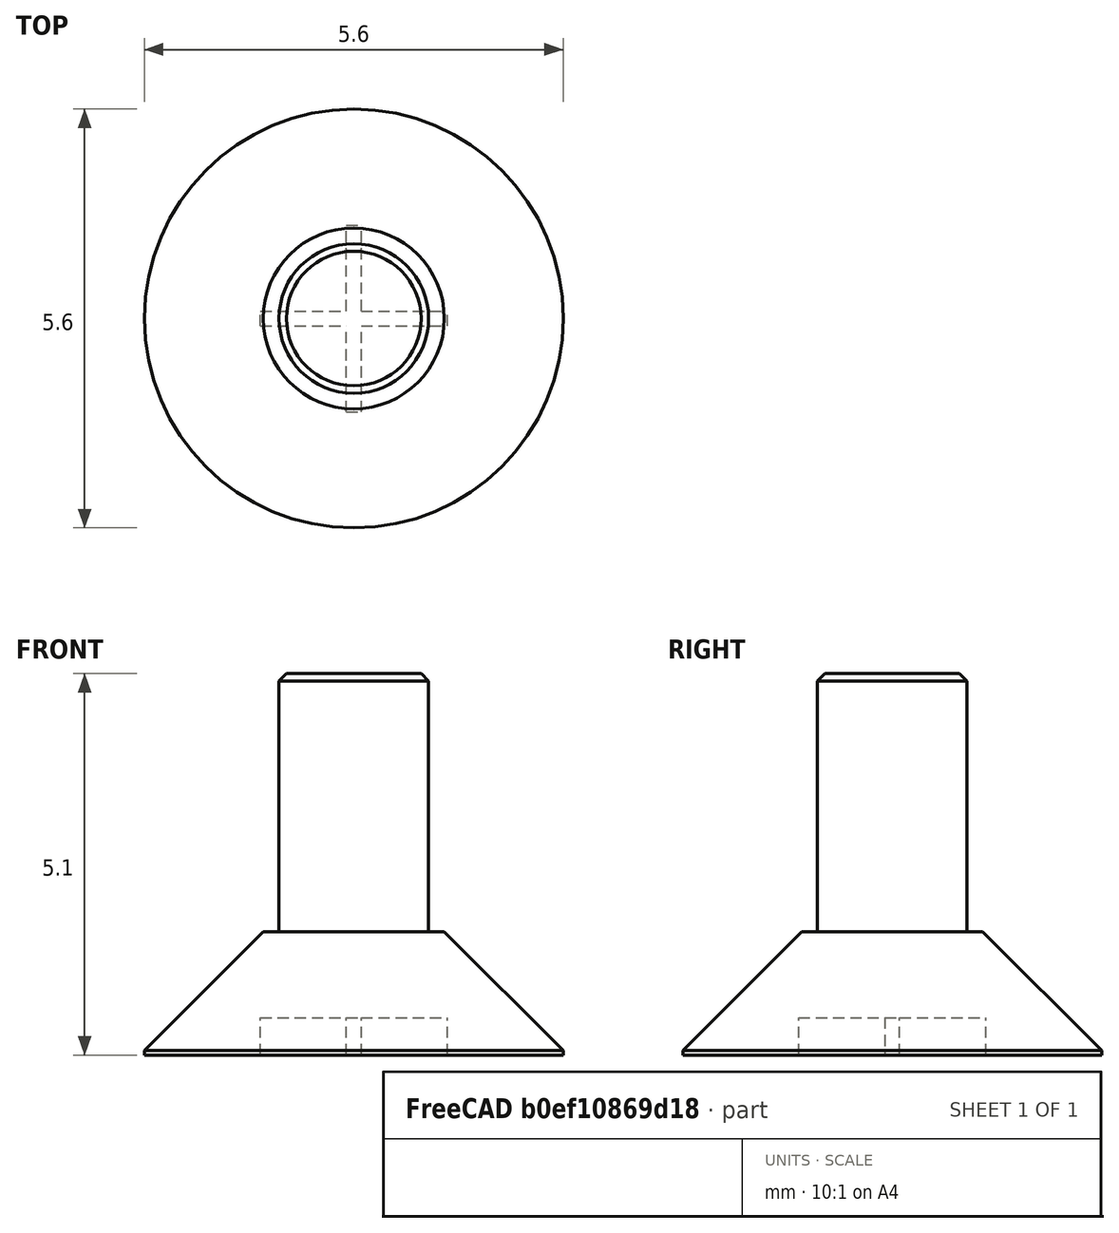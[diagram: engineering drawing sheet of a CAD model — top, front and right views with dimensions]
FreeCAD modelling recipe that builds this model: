
FCSTD DOCUMENT  (FreeCAD 0.16R6706 (Git))
Label: Screw_M3x5
License: All rights reserved
LicenseURL: http://en.wikipedia.org/wiki/All_rights_reserved
objects: Part::Cylinder×2, Part::Box×2, Part::MultiFuse×2, PartDesign::Chamfer×2, Part::Cut×1
note: 9 computed .brp shape members not serialized (recipe doc carries the construction recipe); baked Part::Feature solids carry a one-line shape summary decoded from their .brp

FEATURE [Part::Cylinder] Cylinder  label="Zylinder"
  Angle = 360
  Height = 1.65
  Radius = 2.8
FEATURE [Part::Cylinder] Cylinder001  label="Zylinder001"
  Angle = 360
  Height = 5
  Placement = pos=(0,0,0.1) rot=(0,0,1;0rad)
  Radius = 1
FEATURE [Part::Box] Box  label="Würfel"
  Height = 0.5
  Length = 0.2
  Placement = pos=(-0.1,-1.25,0) rot=(0,0,1;0rad)
  Width = 2.5
FEATURE [Part::Box] Box001  label="Würfel001"
  Height = 0.5
  Length = 2.5
  Placement = pos=(-1.25,-0.1,0) rot=(0,0,1;0rad)
  Width = 0.2
FEATURE [Part::MultiFuse] Fusion
  Shapes = -> [Box001,Box]
FEATURE [Part::MultiFuse] Fusion001
  Shapes = -> [Cylinder001,Cylinder]
FEATURE [Part::Cut] Cut
  Base = -> Fusion001
  Tool = -> Fusion
FEATURE [PartDesign::Chamfer] Chamfer
  Base = -> Cut [Edge4]
  Size = 1.59
FEATURE [PartDesign::Chamfer] Chamfer001  label="SCREW"
  Base = -> Chamfer [Edge6]
  Size = 0.1
